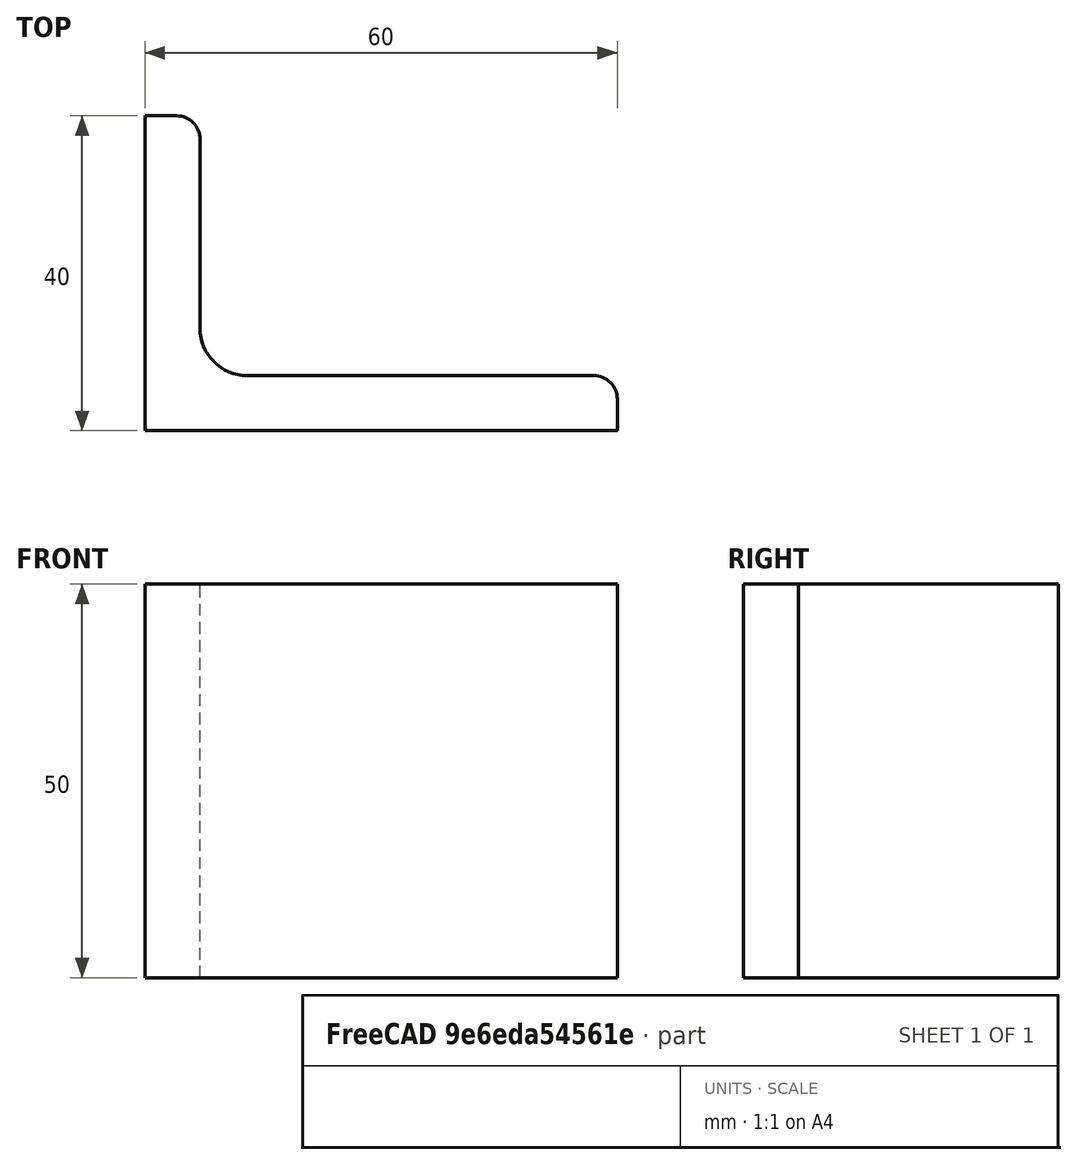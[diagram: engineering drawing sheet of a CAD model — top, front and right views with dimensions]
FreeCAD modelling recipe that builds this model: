
FCSTD DOCUMENT  (FreeCAD 0.15R4671 (Git))
Label: Angle Bar 60x40x7 EN10056 S235JR
License: All rights reserved
LicenseURL: http://en.wikipedia.org/wiki/All_rights_reserved
objects: Sketcher::SketchObject×1, Part::Extrusion×1
note: 2 computed .brp shape members not serialized (recipe doc carries the construction recipe); baked Part::Feature solids carry a one-line shape summary decoded from their .brp

FEATURE [Sketcher::SketchObject] Sketch
  sketch-geometry (9):
    g0: LineSegment StartX=0 StartY=0 StartZ=0 EndX=60 EndY=0 EndZ=0
    g1: LineSegment StartX=60 StartY=0 StartZ=0 EndX=60 EndY=4 EndZ=0
    g2: LineSegment StartX=57 StartY=7 StartZ=0 EndX=13 EndY=7 EndZ=0
    g3: LineSegment StartX=0 StartY=0 StartZ=0 EndX=0 EndY=40 EndZ=0
    g4: LineSegment StartX=0 StartY=40 StartZ=0 EndX=4 EndY=40 EndZ=0
    g5: LineSegment StartX=7 StartY=37 StartZ=0 EndX=7 EndY=13 EndZ=0
    g6: ArcOfCircle CenterX=13 CenterY=13 CenterZ=0 NormalX=0 NormalY=0 NormalZ=1 Radius=6 StartAngle=3.14159 EndAngle=4.71239
    g7: ArcOfCircle CenterX=4 CenterY=37 CenterZ=0 NormalX=0 NormalY=0 NormalZ=1 Radius=3 StartAngle=0 EndAngle=1.5708
    g8: ArcOfCircle CenterX=57 CenterY=4 CenterZ=0 NormalX=0 NormalY=0 NormalZ=1 Radius=3 StartAngle=0 EndAngle=1.5708
  constraints (23):
    c: Coincident(g0,g-1)
    c: Horizontal(g0)
    c: Coincident(g1,g0)
    c: Vertical(g1)
    c: Horizontal(g2)
    c: Coincident(g3,g-1)
    c: Vertical(g3)
    c: Coincident(g4,g3)
    c: Horizontal(g4)
    c: Vertical(g5)
    c: Tangent(g5,g6) = -1.5708
    c: Tangent(g2,g6) = 1.5708
    c: Tangent(g4,g7) = 1.5708
    c: Tangent(g5,g7) = 1.5708
    c: Tangent(g2,g8) = -1.5708
    c: Tangent(g1,g8) = -1.5708
    c: DistanceX(g0) = 60
    c: DistanceY(g3) = 40
    c: DistanceY(g0,g2) = 7
    c: DistanceX(g3,g5) = 7
    c: Radius(g6) = 6
    c: Radius(g8) = 3
    c: Radius(g7) = 3
FEATURE [Part::Extrusion] Extrude  label="Angle Bar 60x40x7 EN10056 S235JR"
  Base = -> Sketch
  Dir = (0,0,50)
  Solid = true
